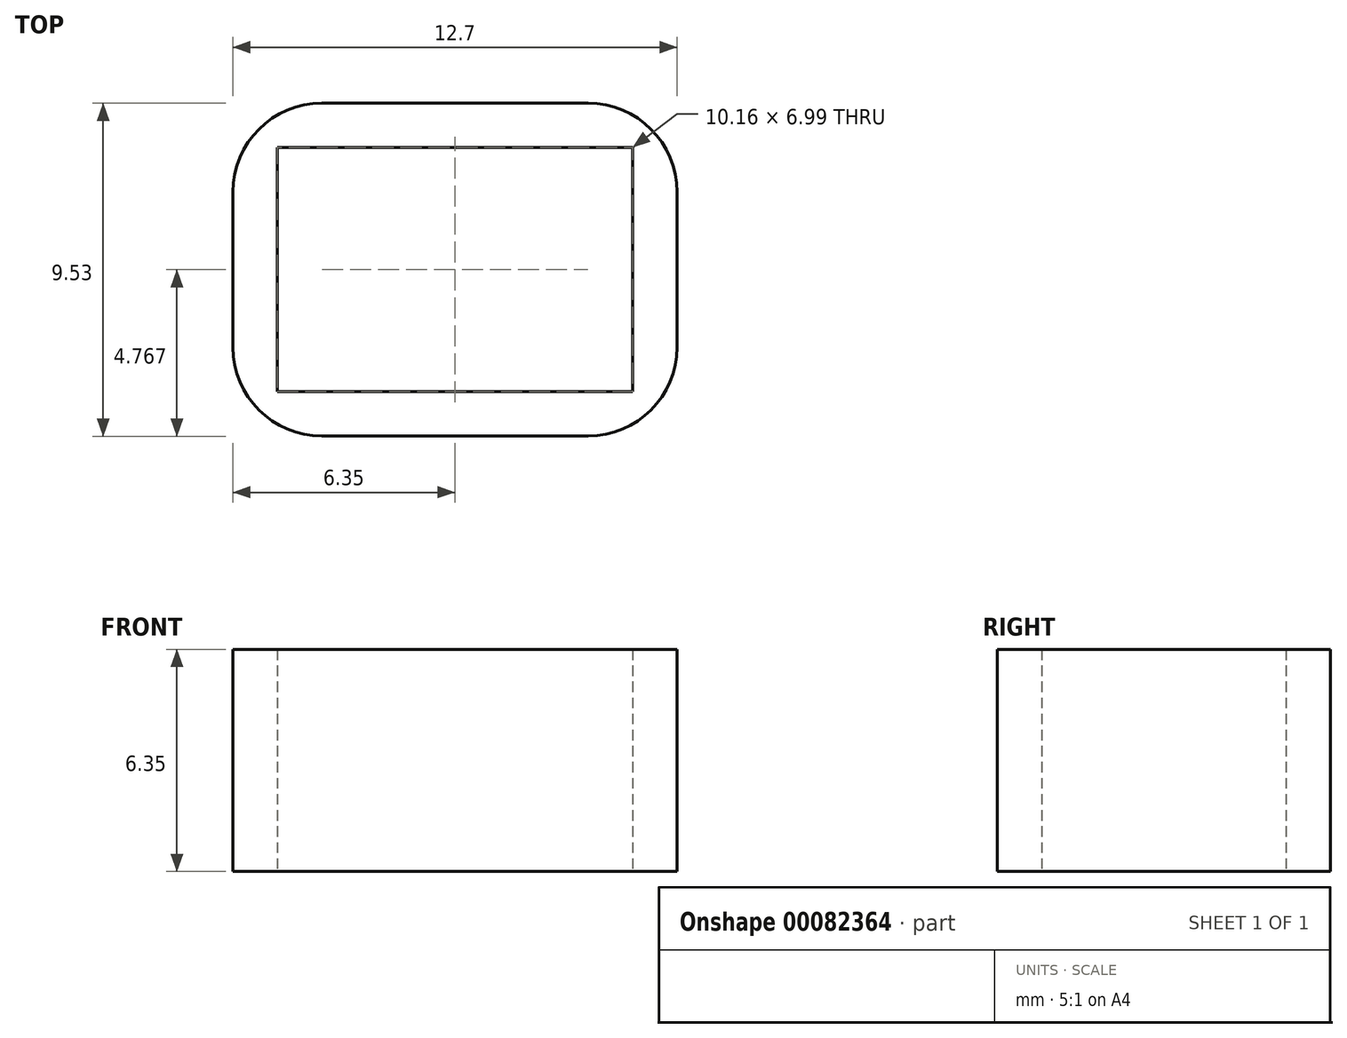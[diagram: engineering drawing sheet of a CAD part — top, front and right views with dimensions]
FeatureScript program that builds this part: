
annotation { "Feature Type Name" : "Feature", "Feature Type Description" : "" }
export const myFeature = defineFeature(function(context is Context, id is Id, definition is map)
    precondition{}
    {
        {
            var Q0;
            Q0=qCreatedBy(makeId("Top.planeOp"),FACE);
            var sketch = newSketch(context, id + "F0", { "sketchPlane" : qUnion([Q0])});
            skLineSegment(sketch, "E0.bottom", {"start": v(0, 0) * mm, "end": v(12.7, 0) * mm});
            skLineSegment(sketch, "E0.top", {"start": v(0, -9.52) * mm, "end": v(12.7, -9.52) * mm});
            skLineSegment(sketch, "E0.left", {"start": v(0, 0) * mm, "end": v(0, -9.52) * mm});
            skLineSegment(sketch, "E0.right", {"start": v(12.7, 0) * mm, "end": v(12.7, -9.53) * mm});
            skLineSegment(sketch, "E1.0", {"start": v(0, -2524.12) * mm, "end": v(12.7, -2524.12) * mm});
            skLineSegment(sketch, "E2.0", {"start": v(11.43, -1.27) * mm, "end": v(11.43, -8.25) * mm});
            skLineSegment(sketch, "E3.0", {"start": v(1.27, -1.27) * mm, "end": v(11.43, -1.27) * mm});
            skLineSegment(sketch, "E4.0", {"start": v(1.27, -8.25) * mm, "end": v(11.43, -8.25) * mm});
            skLineSegment(sketch, "E5.0", {"start": v(1.27, -1.27) * mm, "end": v(1.27, -8.25) * mm});
            skSolve(sketch);
        }
        {
            var Q0;
            Q0=makeQuery(id+"F0.imprint","IMPRINT",FACE,{"disambiguationData":[TD([[makeQuery(id+"F0.imprint","IMPRINT",EDGE,{"derivedFrom":sQuery(id+"F0.wireOp",EDGE,"E0.bottom")}),-1.0]])]});
            extrude(context, id + "F1", {"entities" : qUnion([Q0]), "depth" : 6.35 * mm});
        }
        {
            var Q0;
            Q0=makeQuery(id+"F1.opExtrude","SWEPT_EDGE",EDGE,{"disambiguationData":[OSD([sQuery(id+"F0.wireOp",EDGE,"E0.top"),sQuery(id+"F0.wireOp",EDGE,"E0.right")])]});
            fillet(context, id + "F2", {"entities" : qUnion([Q0]), "radius" : 2.54 * mm, "tangentPropagation" : true, "allowEdgeOverflow" : false});
        }
        {
            var Q0;
            Q0=makeQuery(id+"F1.opExtrude","SWEPT_EDGE",EDGE,{"disambiguationData":[OSD([sQuery(id+"F0.wireOp",EDGE,"E0.top"),sQuery(id+"F0.wireOp",EDGE,"E0.left")])]});
            fillet(context, id + "F3", {"entities" : qUnion([Q0]), "radius" : 2.54 * mm, "tangentPropagation" : true, "allowEdgeOverflow" : false});
        }
        {
            var Q0;
            Q0=makeQuery(id+"F1.opExtrude","SWEPT_EDGE",EDGE,{"disambiguationData":[OSD([sQuery(id+"F0.wireOp",EDGE,"E0.bottom"),sQuery(id+"F0.wireOp",EDGE,"E0.right")])]});
            var Q1;
            Q1=makeQuery(id+"F1.opExtrude","SWEPT_EDGE",EDGE,{"disambiguationData":[OSD([sQuery(id+"F0.wireOp",EDGE,"E0.bottom"),sQuery(id+"F0.wireOp",EDGE,"E0.left")])]});
            fillet(context, id + "F4", {"entities" : qUnion([Q0, Q1]), "radius" : 2.54 * mm, "tangentPropagation" : true, "allowEdgeOverflow" : false});
        }
    });
